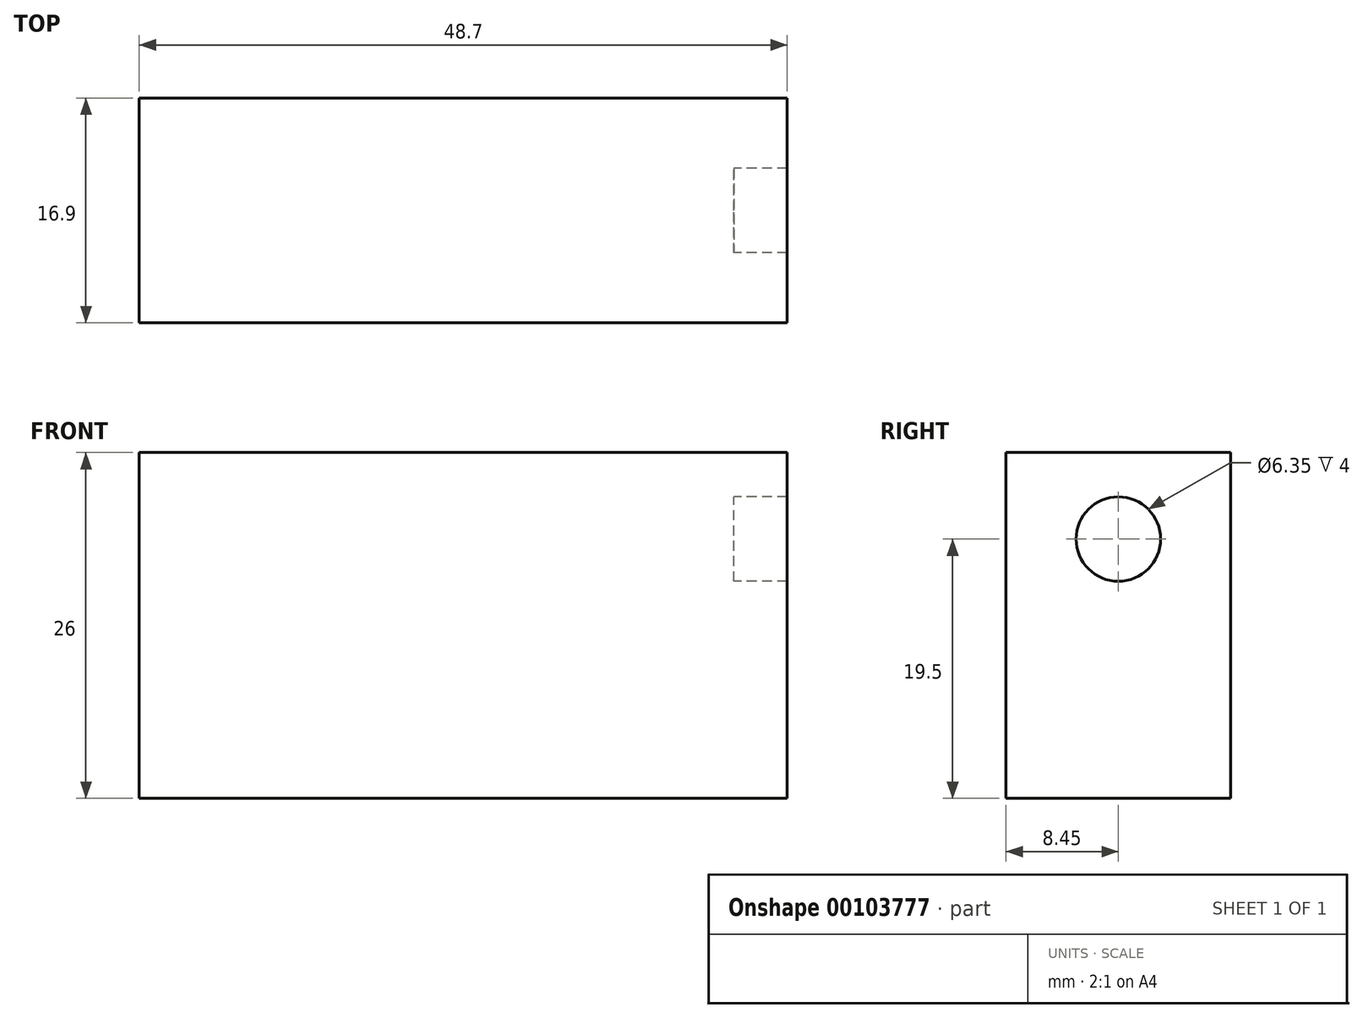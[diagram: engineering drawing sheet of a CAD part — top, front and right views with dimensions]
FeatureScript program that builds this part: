
annotation { "Feature Type Name" : "Feature", "Feature Type Description" : "" }
export const myFeature = defineFeature(function(context is Context, id is Id, definition is map)
    precondition{}
    {
        {
            var Q0;
            Q0=qCreatedBy(makeId("Front.planeOp"),FACE);
            var sketch = newSketch(context, id + "F0", { "sketchPlane" : qUnion([Q0])});
            skLineSegment(sketch, "E0.bottom", {"start": v(22.35, 13) * mm, "end": v(-22.35, 13) * mm});
            skLineSegment(sketch, "E0.top", {"start": v(22.35, -13) * mm, "end": v(-22.35, -13) * mm});
            skLineSegment(sketch, "E0.left", {"start": v(22.35, 13) * mm, "end": v(22.35, -13) * mm});
            skLineSegment(sketch, "E0.right", {"start": v(-22.35, 13) * mm, "end": v(-22.35, -13) * mm});
            skPoint(sketch, "E0.middle", {"position": v(0, 0) * mm});
            skSolve(sketch);
        }
        {
            var Q0;
            Q0=makeQuery(id+"F0.imprint","IMPRINT",FACE,{"disambiguationData":[TD([[makeQuery(id+"F0.imprint","IMPRINT",EDGE,{"derivedFrom":sQuery(id+"F0.wireOp",EDGE,"E0.bottom")}),1.0]])]});
            extrude(context, id + "F1", {"entities" : qUnion([Q0]), "depth" : 16.9 * mm});
        }
        {
            var Q0;
            Q0=makeQuery(id+"F1.opExtrude","SWEPT_FACE",FACE,{"disambiguationData":[OSD([sQuery(id+"F0.wireOp",EDGE,"E0.left")])]});
            var sketch = newSketch(context, id + "F2", { "sketchPlane" : qUnion([Q0])});
            skLineSegment(sketch, "E1", {"start": v(-8.45, -13) * mm, "end": v(-8.45, 13) * mm});
            skLineSegment(sketch, "E2", {"start": v(-8.45, 0) * mm, "end": v(-8.45, 6.5) * mm});
            skLineSegment(sketch, "E3", {"start": v(-16.9, 0) * mm, "end": v(0, 0) * mm});
            skCircle(sketch, "E4", {"center": v(-8.45, 6.5) * mm, "radius": 3.18 * mm});
            skCircle(sketch, "E5.MirrorC", {"center": v(-8.45, -6.5) * mm, "radius": 3.18 * mm});
            skSolve(sketch);
        }
        {
            var Q0;
            {var subQ0=sQuery(id+"F2.wireOp",EDGE,"E5.MirrorC");var subQ1=sQuery(id+"F2.wireOp",EDGE,"E1");var subQ2=makeQuery(id+"F2.imprint","INTERSECT",VERTEX,{"disambiguationData":[OD(0.0)],"derivedFrom":[subQ1,subQ0]});Q0=makeQuery(id+"F2.imprint","IMPRINT",FACE,{"disambiguationData":[TD([[makeQuery(id+"F2.imprint","IMPRINT",EDGE,{"disambiguationData":[TD([[subQ2,-1.0]])],"derivedFrom":subQ1}),1.0]])]});}
            var Q1;
            {var subQ0=sQuery(id+"F2.wireOp",EDGE,"E5.MirrorC");var subQ1=sQuery(id+"F2.wireOp",EDGE,"E1");var subQ2=makeQuery(id+"F2.imprint","INTERSECT",VERTEX,{"disambiguationData":[OD(0.0)],"derivedFrom":[subQ1,subQ0]});Q1=makeQuery(id+"F2.imprint","IMPRINT",FACE,{"disambiguationData":[TD([[makeQuery(id+"F2.imprint","IMPRINT",EDGE,{"disambiguationData":[TD([[subQ2,-1.0]])],"derivedFrom":subQ1}),-1.0]])]});}
            var Q2;
            {var subQ0=sQuery(id+"F2.wireOp",EDGE,"E2");var subQ1=sQuery(id+"F2.wireOp",EDGE,"E1");var subQ2=makeQuery(id+"F2.imprint","INTERSECT",VERTEX,{"derivedFrom":[subQ1,subQ0]});Q2=makeQuery(id+"F2.imprint","IMPRINT",FACE,{"disambiguationData":[TD([[makeQuery(id+"F2.imprint","IMPRINT",EDGE,{"disambiguationData":[TD([[subQ2,-1.0]])],"derivedFrom":subQ1}),1.0]])]});}
            var Q3;
            {var subQ0=sQuery(id+"F2.wireOp",EDGE,"E2");var subQ1=sQuery(id+"F2.wireOp",EDGE,"E1");var subQ2=makeQuery(id+"F2.imprint","INTERSECT",VERTEX,{"derivedFrom":[subQ1,subQ0]});Q3=makeQuery(id+"F2.imprint","IMPRINT",FACE,{"disambiguationData":[TD([[makeQuery(id+"F2.imprint","IMPRINT",EDGE,{"disambiguationData":[TD([[subQ2,-1.0]])],"derivedFrom":subQ1}),-1.0]])]});}
            extrude(context, id + "F3", {"entities" : qUnion([Q0, Q1, Q2, Q3]), "operationType" : NewBodyOperationType.ADD, "depth" : 4 * mm});
        }
    });
